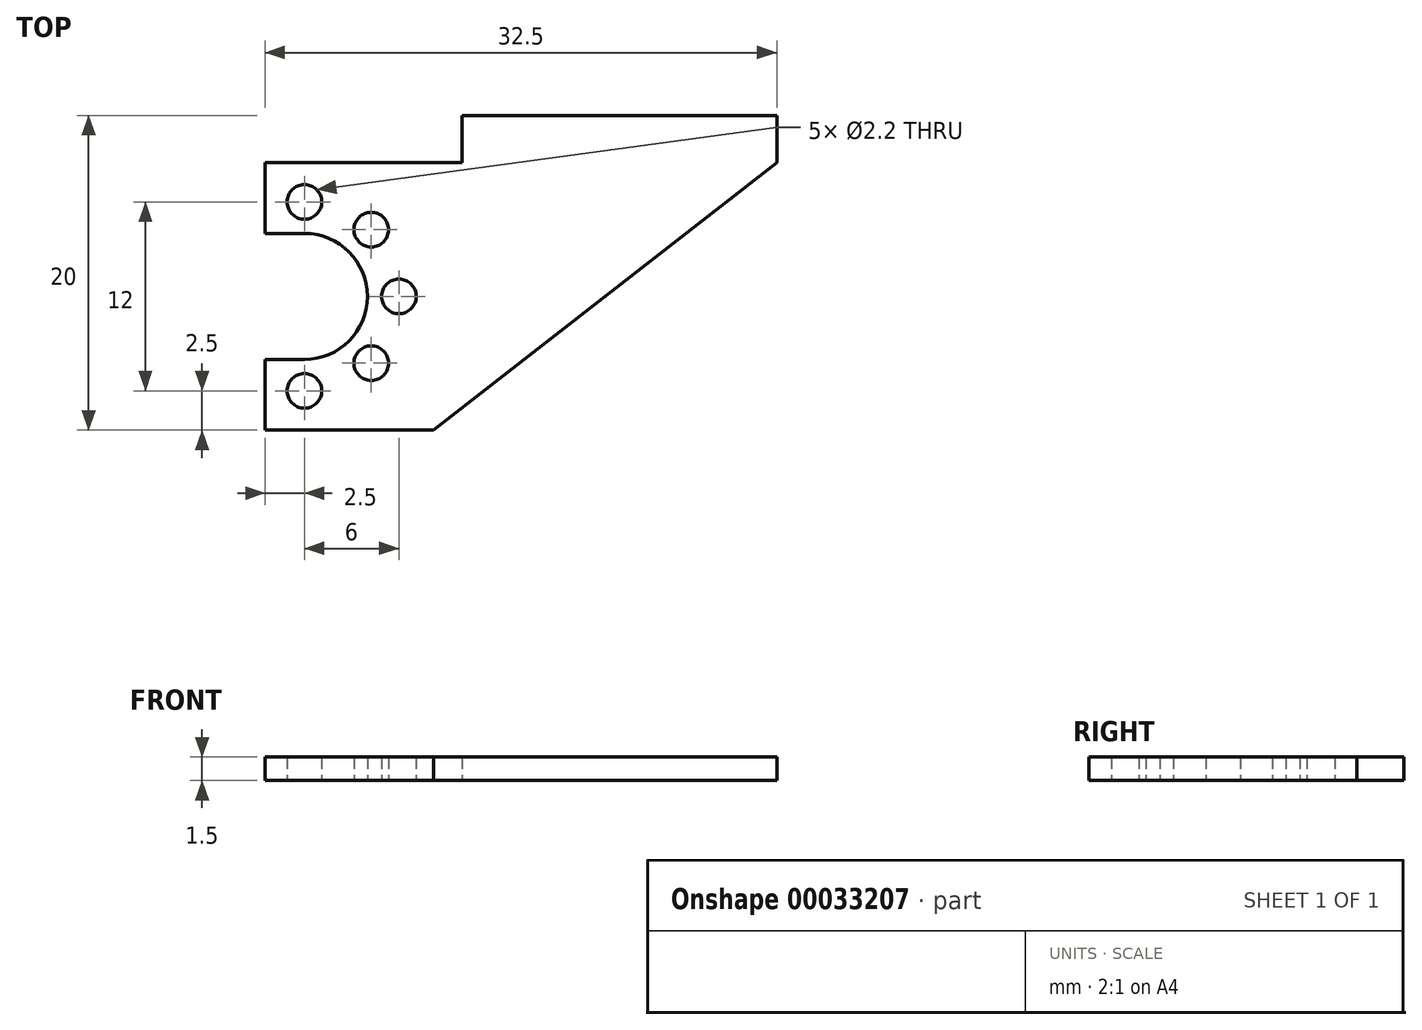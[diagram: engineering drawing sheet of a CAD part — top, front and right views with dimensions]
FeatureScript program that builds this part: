
annotation { "Feature Type Name" : "Feature", "Feature Type Description" : "" }
export const myFeature = defineFeature(function(context is Context, id is Id, definition is map)
    precondition{}
    {
        {
            var Q0;
            Q0=qCreatedBy(makeId("Top.planeOp"),FACE);
            var sketch = newSketch(context, id + "F0", { "sketchPlane" : qUnion([Q0])});
            skLineSegment(sketch, "E0.bottom", {"start": v(16.25, 8.5) * mm, "end": v(-16.25, 8.5) * mm});
            skLineSegment(sketch, "E0.top", {"start": v(-5.55, -8.5) * mm, "end": v(-16.25, -8.5) * mm});
            skLineSegment(sketch, "E0.right", {"start": v(-16.25, 8.5) * mm, "end": v(-16.25, 4) * mm});
            skPoint(sketch, "E0.middle", {"position": v(0, 0) * mm});
            skArc(sketch, "E1", {"start": v(-13.75, -4) * mm, "mid": v(-9.75, 0) * mm, "end": v(-13.75, 4) * mm});
            skCircle(sketch, "E2", {"center": v(-13.75, -6) * mm, "radius": 1.1 * mm});
            skCircle(sketch, "E3.1.0", {"center": v(-9.5, -4.24) * mm, "radius": 1.1 * mm});
            skCircle(sketch, "E3.2.0", {"center": v(-7.75, 0) * mm, "radius": 1.1 * mm});
            skCircle(sketch, "E3.3.0", {"center": v(-9.5, 4.24) * mm, "radius": 1.1 * mm});
            skCircle(sketch, "E3.4.0", {"center": v(-13.75, 6) * mm, "radius": 1.1 * mm});
            skLineSegment(sketch, "E4", {"start": v(-13.75, 4) * mm, "end": v(-16.25, 4) * mm});
            skLineSegment(sketch, "E5", {"start": v(-13.75, -4) * mm, "end": v(-16.25, -4) * mm});
            skLineSegment(sketch, "E6.trimOffspring", {"start": v(-16.25, -4) * mm, "end": v(-16.25, -8.5) * mm});
            skLineSegment(sketch, "E7", {"start": v(-5.55, -8.5) * mm, "end": v(16.25, 8.5) * mm});
            skPoint(sketch, "E8.orphan", {"position": v(16.25, -8.5) * mm});
            skSolve(sketch);
        }
        {
            var Q0;
            Q0 = qSketchRegion(id + "F0", true);
            extrude(context, id + "F1", {"entities" : qUnion([Q0]), "depth" : 1.5 * mm});
        }
        {
            var Q0;
            Q0=makeQuery(id+"F1.opExtrude","SWEPT_FACE",FACE,{"disambiguationData":[OSD([sQuery(id+"F0.wireOp",EDGE,"E0.bottom")])]});
            var sketch = newSketch(context, id + "F2", { "sketchPlane" : qUnion([Q0])});
            skLineSegment(sketch, "E9.bottom", {"start": v(-16.25, 1.5) * mm, "end": v(3.75, 1.5) * mm});
            skLineSegment(sketch, "E9.top", {"start": v(-16.25, 0) * mm, "end": v(3.75, 0) * mm});
            skLineSegment(sketch, "E9.left", {"start": v(-16.25, 1.5) * mm, "end": v(-16.25, 0) * mm});
            skLineSegment(sketch, "E9.right", {"start": v(3.75, 1.5) * mm, "end": v(3.75, 0) * mm});
            skSolve(sketch);
        }
        {
            var Q0;
            Q0 = qSketchRegion(id + "F2", true);
            extrude(context, id + "F3", {"entities" : qUnion([Q0]), "operationType" : NewBodyOperationType.ADD, "depth" : 3 * mm});
        }
    });
